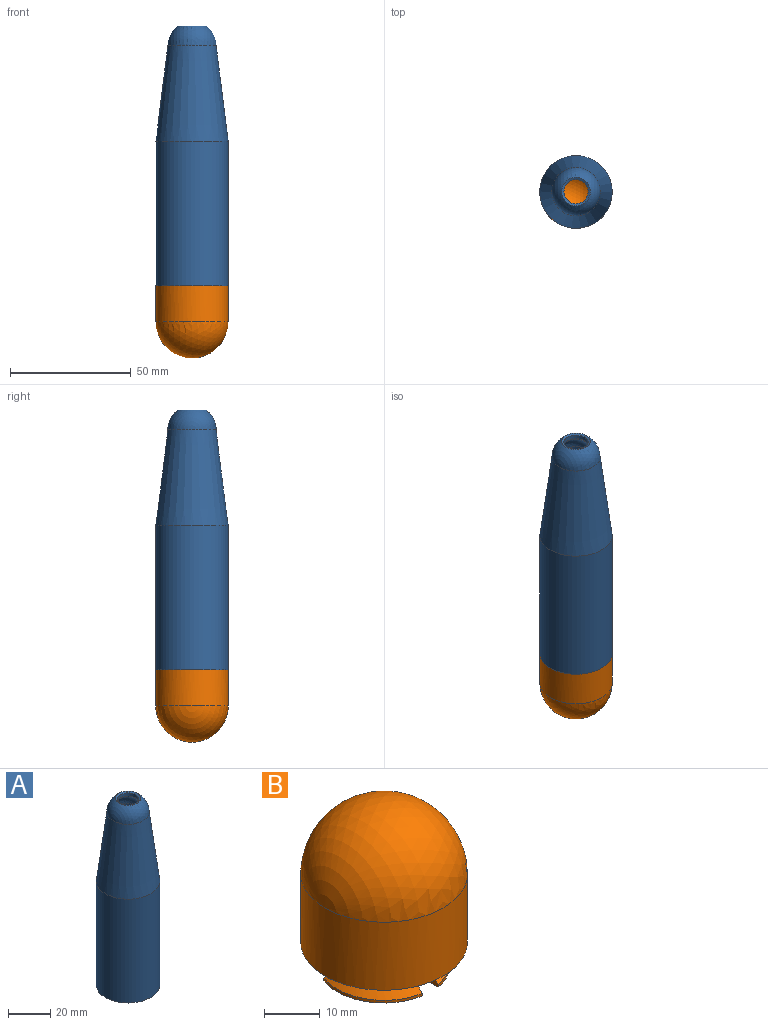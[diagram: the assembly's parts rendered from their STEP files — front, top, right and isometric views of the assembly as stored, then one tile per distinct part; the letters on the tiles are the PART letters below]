
ASSEMBLY  parts=2 mates=1
PART A: 13 faces, bbox 30x30x109.7 mm
  f0: cylinder r=12.5mm len=54.84mm, axis (0,0,1), area 4307.4mm2, adj f4,f6
  f1: plane 30x30mm, normal (0,0,-1), area 216mm2, adj f2,f7
  f2: cylinder r=15mm len=60mm, axis (0,0,1), area 5654.9mm2, adj f1,f3
  f3: cone r=15mm half-angle=7.2deg, axis (0,0,-1), area 3141.6mm2, adj f2,f9
  f4: cone r=12.52mm half-angle=7.2deg, axis (0,0,-1), area 2520.7mm2, adj f0,f8
  f5: cylinder r=10.5mm len=21mm, axis (0,0,-1), area 66mm2, adj f6,f7
  f6: cone r=12.5mm half-angle=45deg, axis (0,0,1), area 204.4mm2, adj f0,f5
  f7: cone r=10.5mm half-angle=45deg, axis (0,0,-1), area 204.4mm2, adj f1,f5
  f8: sphere r=7.48mm, area 253.7mm2, adj f4,f11
  f9: sphere r=10mm, area 506.4mm2, adj f3,f12
  f10: cylinder r=5mm len=10mm, axis (0,0,-1), area 55.9mm2, adj f11,f12
  f11: cone r=5mm half-angle=23.1deg, axis (0,0,-1), area 14.5mm2, adj f8,f10
  f12: cone r=5.92mm half-angle=63.1deg, axis (0,0,1), area 35.3mm2, adj f9,f10
PART B: 26 faces, bbox 30x30x35 mm
  f0: plane 18.34x5.79mm, normal (0,0,-1), area 52.1mm2, adj f4,f19,f23,f24
  f1: plane 15.89x9.91mm, normal (0,0,-1), area 52.1mm2, adj f16,f19,f20,f25
  f2: cylinder r=10.5mm len=15.85mm, axis (0,0,-1), area 18mm2, adj f3,f5,f23,f24
  f3: cone r=12.5mm half-angle=45deg, axis (0,0,1), area 56.7mm2, adj f2,f13,f23,f24
  f4: cylinder r=11.91mm len=18.34mm, axis (0,0,1), area 12.3mm2, adj f0,f5,f23,f24
  f5: cone r=10.5mm half-angle=45deg, axis (0,0,-1), area 38.9mm2, adj f2,f4,f23,f24
  f6: plane 15.89x9.91mm, normal (0,0,-1), area 52.1mm2, adj f9,f19,f21,f22
  f7: cylinder r=10.5mm len=13.73mm, axis (0,0,-1), area 18mm2, adj f8,f10,f21,f22
  f8: cone r=12.5mm half-angle=45deg, axis (0,0,1), area 56.7mm2, adj f7,f13,f21,f22
  f9: cylinder r=11.91mm len=15.89mm, axis (0,0,1), area 12.3mm2, adj f6,f10,f21,f22
  f10: cone r=10.5mm half-angle=45deg, axis (0,0,-1), area 38.9mm2, adj f7,f9,f21,f22
  f11: cylinder r=10.5mm len=13.73mm, axis (0,0,-1), area 18mm2, adj f14,f17,f20,f25
  f12: cylinder r=15mm len=30mm, axis (0,0,-1), area 1413.7mm2, adj f13,f15
  f13: plane 30x30mm, normal (0,0,-1), area 258.2mm2, adj f3,f8,f12,f14,f19,f20,f21,f22
  f14: cone r=12.5mm half-angle=45deg, axis (0,0,1), area 56.7mm2, adj f11,f13,f20,f25
  f15: sphere r=15mm, area 1413.7mm2, adj f12
  f16: cylinder r=11.91mm len=15.89mm, axis (0,0,1), area 12.3mm2, adj f1,f17,f20,f25
  f17: cone r=10.5mm half-angle=45deg, axis (0,0,-1), area 38.9mm2, adj f11,f16,f20,f25
  f18: sphere r=9mm, area 508.9mm2, adj f19
  f19: cylinder r=9mm len=20mm, axis (0,0,-1), area 1070.5mm2, adj f0,f1,f6,f13,f18,f20,f21,f22
  f20: plane 5.03x3.6mm, normal (-1,0,0), area 11.6mm2, adj f1,f11,f13,f14,f16,f17,f19
  f21: plane 5.03x3.6mm, normal (1,0,0), area 11.6mm2, adj f6,f7,f8,f9,f10,f13,f19
  f22: plane 5.03x3.12mm, normal (0.5,0.87,0), area 11.6mm2, adj f6,f7,f8,f9,f10,f13,f19
  f23: plane 5.03x3.12mm, normal (-0.5,-0.87,0), area 11.6mm2, adj f0,f2,f3,f4,f5,f13,f19
  f24: plane 5.03x3.12mm, normal (0.5,-0.87,0), area 11.6mm2, adj f0,f2,f3,f4,f5,f13,f19
  f25: plane 5.03x3.12mm, normal (-0.5,0.87,0), area 11.6mm2, adj f1,f11,f13,f14,f16,f17,f19
PLACE A t=(15,0,0)mm
PLACE B rot(axis=(1,0,0),180deg) t=(0,0,5)mm
MATE fastened B.f2 <-> A.f6  axis (0,0,-1) through (0,0,3)mm
